# Revit family: 3460A_NX_Relay
name_source: partatom
category: Communication Devices
units: mm (PartAtom-declared; Revit-internal decimal feet)

## family parameters
Cut with Voids When Loaded = No
Host = Face
Maintain Annotation Orientation = No
OmniClass Number = 23.85.80.11.27
OmniClass Title = Lighting Controls
Part Type = Normal
Room Calculation Point = No
Round Connector Dimension = Use Diameter
Shared = Yes

## types (1)
- 3460A_NX_Relay
    Assembly Code = D5090
    Black Element = Metal-Nickel
    Blue Element = Metal-Aluminum Anodized Blue
    Certification = Certified to UL 916, UL 924 and cUL
    Default Elevation = 48 "
    Description = NX Panel Relay
    Features = • Compatible with all model NXP panels
• Relays are individually replaceable
• Smart Relay Card self-identifies type automatically to panel
• Each relay includes 1 programmable input for low voltage switches,
photocells, or motion sensors
• Plug-in connector to panel motherboard and a single screw to secure it to
the panel enclosure
• Manual override control button and LED status indication
    Housing Material = Paint - Matte White
    Inrush Withstand = 500A @ 20ms (NXR-3LEM Relay)
    Manufacturer = NX Lighting Controls
    Model = NX Panel Relay
    Operating environment = Location: interior space
Operating temperature: 0°- 50°C (32° - 112°F)
Relative humidity (non-condensing): 10%-90%
    Physical = Mounts inside NXP series panel
Pre-drilled mounting hole for securing relay cards
Individual relay cards - 1P and 2P are equal in size
    Type Comments = NX Panel Relay
    URL = https://www.currentlighting.com
    Warranty = 5-Years Warranty

## geometry (parser evidence)
native form markers: Sweep x3
no freeform markers — native parametric forms only
